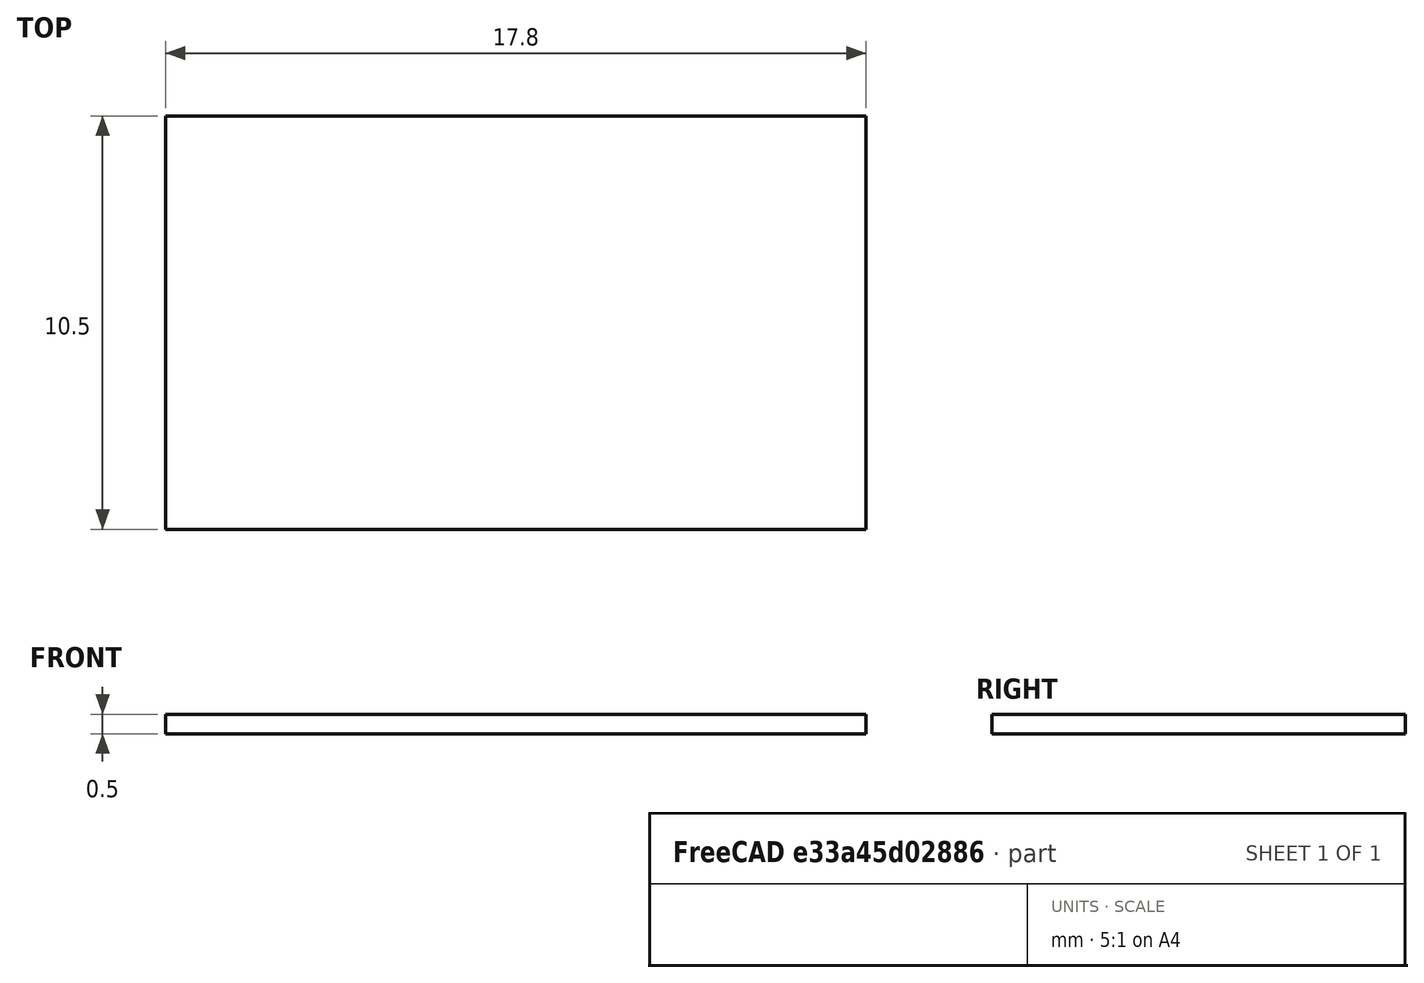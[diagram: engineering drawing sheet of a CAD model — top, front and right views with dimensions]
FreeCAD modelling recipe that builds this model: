
FCSTD DOCUMENT  (FreeCAD 1.0R39285 (Git))
Label: Electronic Shelf Box Label
License: All rights reserved
LicenseURL: https://en.wikipedia.org/wiki/All_rights_reserved
objects: Sketcher::SketchObject×1, PartDesign::Pad×1, PartDesign::Body×1
note: 6 computed .brp shape members not serialized (recipe doc carries the construction recipe); baked Part::Feature solids carry a one-line shape summary decoded from their .brp

FEATURE [Sketcher::SketchObject] Sketch
  ArcFitTolerance = 1e-06
  AttachmentSupport = -> [XY_Plane]
  FullyConstrained = true
  MakeInternals = false
  MapMode = 5
  sketch-geometry (4):
    g0: LineSegment StartX=-8.9 StartY=5.25 StartZ=0 EndX=-8.9 EndY=-5.25 EndZ=0
    g1: LineSegment StartX=-8.9 StartY=-5.25 StartZ=0 EndX=8.9 EndY=-5.25 EndZ=0
    g2: LineSegment StartX=8.9 StartY=-5.25 StartZ=0 EndX=8.9 EndY=5.25 EndZ=0
    g3: LineSegment StartX=8.9 StartY=5.25 StartZ=0 EndX=-8.9 EndY=5.25 EndZ=0
  constraints (11):
    c: Coincident(g0,g1)
    c: Coincident(g1,g2)
    c: Coincident(g2,g3)
    c: Coincident(g3,g0)
    c: Vertical(g0)
    c: Vertical(g2)
    c: Horizontal(g1)
    c: Horizontal(g3)
    c: Distance(g2) = 10.5
    c: Distance(g3) = 17.8
    c: Symmetric(g0,g1,g-1)
FEATURE [PartDesign::Pad] Pad
  Direction = (0,0,1)
  Length = 0.5
  Length2 = 10
  Profile = -> Sketch
  ReferenceAxis = -> Sketch [N_Axis]
  Refine = true
  Suppressed = false
  Type = 0
FEATURE [PartDesign::Body] Body
  AllowCompound = false
  Group = -> [Sketch,Pad]
  Origin = -> Origin
  Tip = -> Pad
